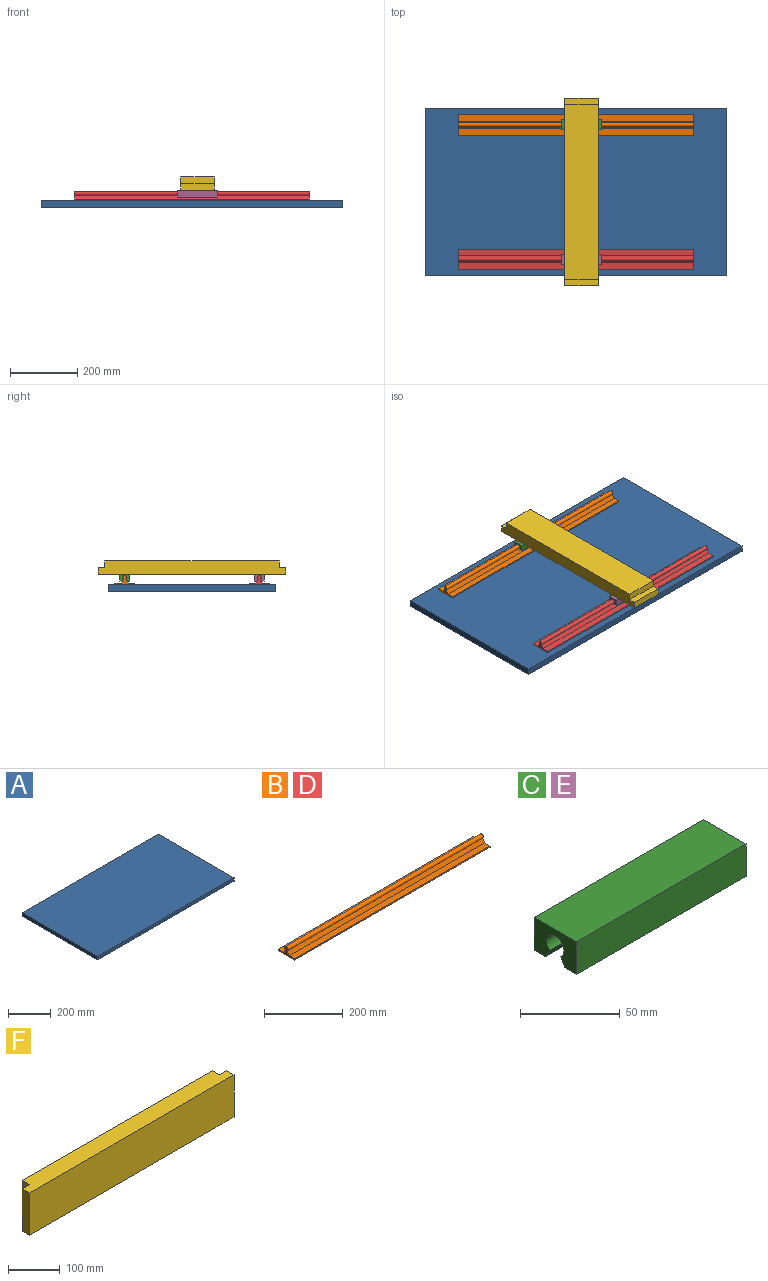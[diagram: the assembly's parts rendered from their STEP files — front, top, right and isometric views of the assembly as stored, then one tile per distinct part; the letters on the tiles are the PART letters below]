
ASSEMBLY  parts=6 mates=6
PART A: 6 faces, bbox 900x500x20 mm
  f0: plane 500x20mm, normal (-1,0,0), area 10000mm2, adj f1,f3,f4,f5
  f1: plane 900x20mm, normal (0,-1,0), area 18000mm2, adj f0,f2,f4,f5
  f2: plane 500x20mm, normal (1,0,0), area 10000mm2, adj f1,f3,f4,f5
  f3: plane 900x20mm, normal (0,1,0), area 18000mm2, adj f0,f2,f4,f5
  f4: plane 900x500mm, normal (0,0,1), area 450000mm2, adj f0,f1,f2,f3
  f5: plane 900x500mm, normal (0,0,-1), area 450000mm2, adj f0,f1,f2,f3
PART B: 10 faces, bbox 700x60x26 mm
  f0: cylinder r=6mm len=700mm, axis (-1,0,0), area 20584.6mm2, adj f1,f7,f8,f9
  f1: plane 700x11.38mm, normal (0,-0.87,0.5), area 9195.5mm2, adj f0,f2,f8,f9
  f2: plane 700x19.61mm, normal (0,0,1), area 13725.4mm2, adj f1,f3,f8,f9
  f3: plane 700x4mm, normal (0,-1,0), area 2800mm2, adj f2,f4,f8,f9
  f4: plane 700x60mm, normal (0,0,-1), area 42000mm2, adj f3,f5,f8,f9
  f5: plane 700x4mm, normal (0,1,0), area 2800mm2, adj f4,f6,f8,f9
  f6: plane 700x19.61mm, normal (0,0,1), area 13725.4mm2, adj f5,f7,f8,f9
  f7: plane 700x11.38mm, normal (0,0.87,0.5), area 9195.5mm2, adj f0,f6,f8,f9
  f8: plane 60x26mm, normal (1,0,0), area 507.6mm2, adj f0,f1,f2,f3,f4,f5,f6,f7
  f9: plane 60x26mm, normal (-1,0,0), area 507.6mm2, adj f0,f1,f2,f3,f4,f5,f6,f7
PART C: 10 faces, bbox 120x30x20 mm
  f0: cylinder r=6mm len=120mm, axis (-1,0,0), area 3528.8mm2, adj f1,f7,f8,f9
  f1: plane 120x5.38mm, normal (0,-0.87,-0.5), area 745mm2, adj f0,f2,f8,f9
  f2: plane 120x8.07mm, normal (0,0,-1), area 968.6mm2, adj f1,f3,f8,f9
  f3: plane 120x20mm, normal (0,1,0), area 2400mm2, adj f2,f4,f8,f9
  f4: plane 120x30mm, normal (0,0,1), area 3600mm2, adj f3,f5,f8,f9
  f5: plane 120x20mm, normal (0,-1,0), area 2400mm2, adj f4,f6,f8,f9
  f6: plane 120x8.07mm, normal (0,0,-1), area 968.6mm2, adj f5,f7,f8,f9
  f7: plane 120x5.38mm, normal (0,0.87,-0.5), area 745mm2, adj f0,f6,f8,f9
  f8: plane 30x20mm, normal (1,0,0), area 436.3mm2, adj f0,f1,f2,f3,f4,f5,f6,f7
  f9: plane 30x20mm, normal (-1,0,0), area 436.3mm2, adj f0,f1,f2,f3,f4,f5,f6,f7
PART D: same geometry as B
PART E: same geometry as C
PART F: 10 faces, bbox 560x40x100 mm
  f0: plane 100x20mm, normal (0,1,0), area 2000mm2, adj f1,f2,f4,f8
  f1: plane 100x20mm, normal (-1,0,0), area 2000mm2, adj f0,f2,f4,f5
  f2: plane 560x40mm, normal (0,0,-1), area 21600mm2, adj f0,f1,f3,f5,f6,f7,f8,f9
  f3: plane 100x20mm, normal (1,0,0), area 2000mm2, adj f2,f4,f5,f6
  f4: plane 560x40mm, normal (0,0,1), area 21600mm2, adj f0,f1,f3,f5,f6,f7,f8,f9
  f5: plane 560x100mm, normal (0,-1,0), area 56000mm2, adj f1,f2,f3,f4
  f6: plane 100x20mm, normal (0,1,0), area 2000mm2, adj f2,f3,f4,f7
  f7: plane 100x20mm, normal (1,0,0), area 2000mm2, adj f2,f4,f6,f9
  f8: plane 100x20mm, normal (-1,0,0), area 2000mm2, adj f0,f2,f4,f9
  f9: plane 520x100mm, normal (0,1,0), area 52000mm2, adj f2,f4,f7,f8
PLACE A rot(axis=(0,0,1),180deg) t=(404.71,915.56,1091.16)mm
PLACE B t=(404.71,1115.56,1121.16)mm
PLACE C rot(axis=(-0.15,0,0.99),0deg) t=(421.24,1115.56,1121.16)mm
PLACE D t=(404.71,715.56,1121.16)mm
PLACE E rot(axis=(-0.23,0.02,0.97),0deg) t=(421.24,715.56,1121.16)mm
PLACE F rot(axis=(0.58,-0.58,-0.58),120deg) t=(421.24,915.56,1151.16)mm
MATE fastened C.f4 <-> F.f5  axis (0,0,1) through (421.24,1115.56,1131.16)mm
MATE slider D.f0 <-> E.f0  axis (-1,0,0) through (404.71,715.56,1121.16)mm
MATE fastened E.f4 <-> F.f5  axis (0,0,1) through (421.24,715.56,1131.16)mm
MATE fastened A.f4 <-> D.f4  axis (0,0,1) through (404.71,915.56,1101.16)mm
MATE slider B.f0 <-> C.f0  axis (-1,0,0) through (404.71,1115.56,1121.16)mm
MATE fastened A.f4 <-> B.f4  axis (0,0,1) through (404.71,915.56,1101.16)mm
